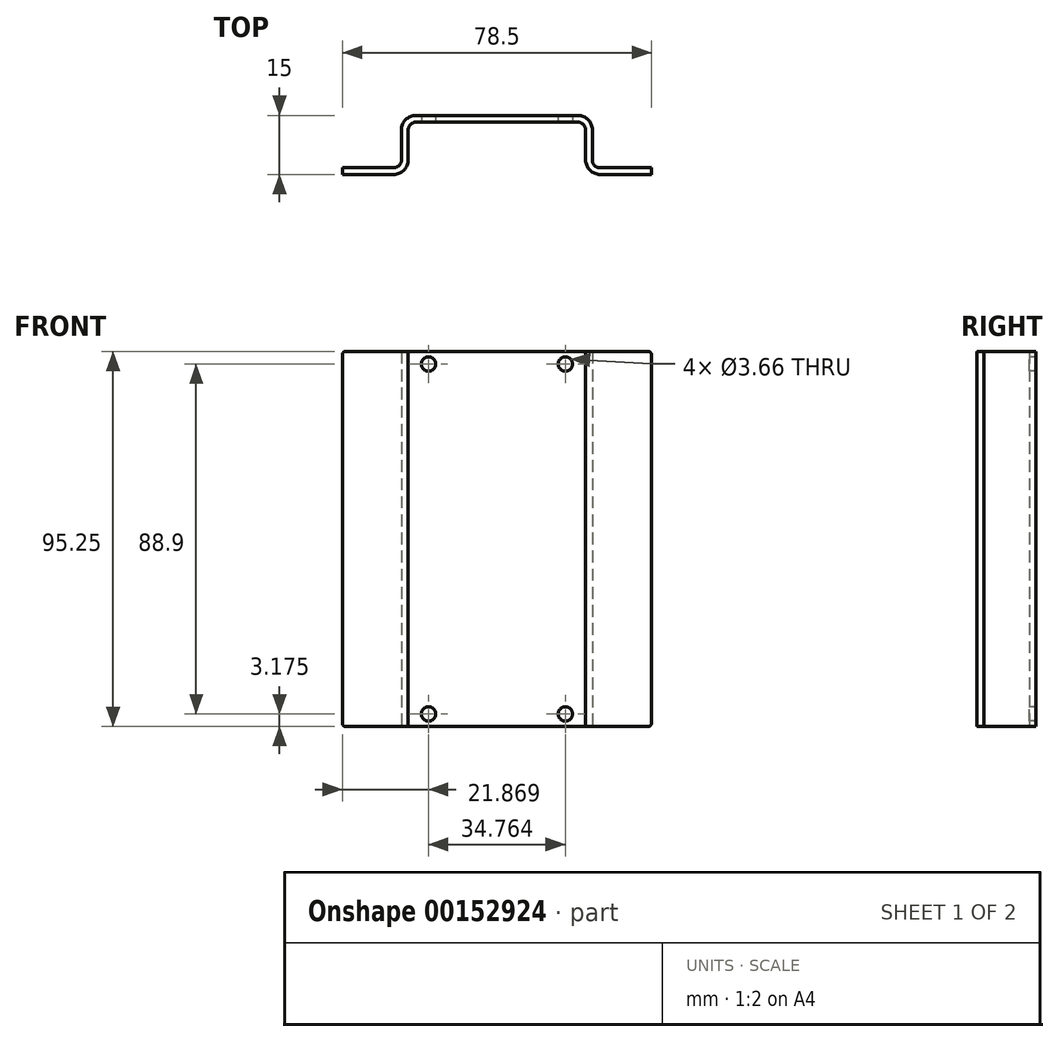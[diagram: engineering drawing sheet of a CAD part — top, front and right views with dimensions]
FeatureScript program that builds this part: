
annotation { "Feature Type Name" : "Feature", "Feature Type Description" : "" }
export const myFeature = defineFeature(function(context is Context, id is Id, definition is map)
    precondition{}
    {
        {
            var Q0;
            Q0=qCreatedBy(makeId("Top.planeOp"),FACE);
            var sketch = newSketch(context, id + "F0", { "sketchPlane" : qUnion([Q0])});
            skLineSegment(sketch, "E0.left", {"start": v(0, 0) * mm, "end": v(0, -13.3) * mm});
            skLineSegment(sketch, "E0.right", {"start": v(-1.7, 1.7) * mm, "end": v(-1.7, -11.58) * mm});
            skLineSegment(sketch, "E1.bottom", {"start": v(-1.7, -11.58) * mm, "end": v(-16.7, -11.58) * mm});
            skLineSegment(sketch, "E1.top", {"start": v(0, -13.3) * mm, "end": v(-16.7, -13.3) * mm});
            skLineSegment(sketch, "E1.right", {"start": v(-16.7, -11.58) * mm, "end": v(-16.7, -13.3) * mm});
            skLineSegment(sketch, "E2.bottom", {"start": v(0, 0) * mm, "end": v(45.08, 0) * mm});
            skLineSegment(sketch, "E2.top", {"start": v(-1.7, 1.7) * mm, "end": v(46.8, 1.7) * mm});
            skLineSegment(sketch, "E3", {"start": v(0, -6.65) * mm, "end": v(-1.7, -6.65) * mm, "construction": true});
            skLineSegment(sketch, "E4.left", {"start": v(45.08, 0) * mm, "end": v(45.08, -13.3) * mm});
            skLineSegment(sketch, "E4.right", {"start": v(46.8, 1.7) * mm, "end": v(46.8, -11.58) * mm});
            skLineSegment(sketch, "E5.bottom", {"start": v(46.8, -11.58) * mm, "end": v(61.8, -11.58) * mm});
            skLineSegment(sketch, "E5.top", {"start": v(45.08, -13.3) * mm, "end": v(61.8, -13.3) * mm});
            skLineSegment(sketch, "E5.right", {"start": v(61.8, -11.58) * mm, "end": v(61.8, -13.3) * mm});
            skLineSegment(sketch, "E6", {"start": v(45.08, -6.65) * mm, "end": v(46.8, -6.65) * mm, "construction": true});
            skLineSegment(sketch, "E7", {"start": v(22.54, 0) * mm, "end": v(22.54, 1.7) * mm, "construction": true});
            skPoint(sketch, "E8", {"position": v(-9.2, -11.58) * mm});
            skPoint(sketch, "E9", {"position": v(54.3, -11.58) * mm});
            skSolve(sketch);
        }
        {
            var Q0;
            Q0=qSketchRegion(id+"F0",true);
            extrude(context, id + "F1", {"entities" : qUnion([Q0]), "depth" : 95.25 * mm});
        }
        {
            var Q0;
            Q0=makeQuery(id+"F1.opExtrude","SWEPT_EDGE",EDGE,{"disambiguationData":[OSD([sQuery(id+"F0.wireOp",EDGE,"E0.left"),sQuery(id+"F0.wireOp",EDGE,"E2.bottom")])]});
            var Q1;
            Q1=makeQuery(id+"F1.opExtrude","SWEPT_EDGE",EDGE,{"disambiguationData":[OSD([sQuery(id+"F0.wireOp",EDGE,"E0.right"),sQuery(id+"F0.wireOp",EDGE,"E1.bottom")])]});
            var Q2;
            Q2=makeQuery(id+"F1.opExtrude","SWEPT_EDGE",EDGE,{"disambiguationData":[OSD([sQuery(id+"F0.wireOp",EDGE,"E2.bottom"),sQuery(id+"F0.wireOp",EDGE,"E4.left")])]});
            var Q3;
            Q3=makeQuery(id+"F1.opExtrude","SWEPT_EDGE",EDGE,{"disambiguationData":[OSD([sQuery(id+"F0.wireOp",EDGE,"E4.right"),sQuery(id+"F0.wireOp",EDGE,"E5.bottom")])]});
            fillet(context, id + "F2", {"entities" : qUnion([Q0, Q1, Q2, Q3]), "radius" : 1.98 * mm, "tangentPropagation" : true, "allowEdgeOverflow" : false});
        }
        {
            var Q0;
            Q0=makeQuery(id+"F1.opExtrude","SWEPT_EDGE",EDGE,{"disambiguationData":[OSD([sQuery(id+"F0.wireOp",EDGE,"E0.left"),sQuery(id+"F0.wireOp",EDGE,"E1.top")])]});
            var Q1;
            Q1=makeQuery(id+"F1.opExtrude","SWEPT_EDGE",EDGE,{"disambiguationData":[OSD([sQuery(id+"F0.wireOp",EDGE,"E0.right"),sQuery(id+"F0.wireOp",EDGE,"E2.top")])]});
            var Q2;
            Q2=makeQuery(id+"F1.opExtrude","SWEPT_EDGE",EDGE,{"disambiguationData":[OSD([sQuery(id+"F0.wireOp",EDGE,"E2.top"),sQuery(id+"F0.wireOp",EDGE,"E4.right")])]});
            var Q3;
            Q3=makeQuery(id+"F1.opExtrude","SWEPT_EDGE",EDGE,{"disambiguationData":[OSD([sQuery(id+"F0.wireOp",EDGE,"E4.left"),sQuery(id+"F0.wireOp",EDGE,"E5.top")])]});
            fillet(context, id + "F3", {"entities" : qUnion([Q0, Q1, Q2, Q3]), "radius" : 3.7 * mm, "tangentPropagation" : true, "allowEdgeOverflow" : false});
        }
        {
            var Q0;
            Q0=makeQuery(id+"F1.opExtrude","CAP_EDGE",EDGE,{"disambiguationData":[OSD([sQuery(id+"F0.wireOp",EDGE,"E1.right")])],"isStart":true});
            var Q1;
            Q1=makeQuery(id+"F1.opExtrude","CAP_EDGE",EDGE,{"disambiguationData":[OSD([sQuery(id+"F0.wireOp",EDGE,"E1.right")])],"isStart":false});
            var Q2;
            Q2=makeQuery(id+"F1.opExtrude","CAP_EDGE",EDGE,{"disambiguationData":[OSD([sQuery(id+"F0.wireOp",EDGE,"E5.right")])],"isStart":true});
            var Q3;
            Q3=makeQuery(id+"F1.opExtrude","CAP_EDGE",EDGE,{"disambiguationData":[OSD([sQuery(id+"F0.wireOp",EDGE,"E5.right")])],"isStart":false});
            fillet(context, id + "F4", {"entities" : qUnion([Q0, Q1, Q2, Q3]), "radius" : 0.76 * mm, "tangentPropagation" : true, "allowEdgeOverflow" : false});
        }
        {
            var Q0;
            Q0=makeQuery(id+"F1.opExtrude","SWEPT_FACE",FACE,{"disambiguationData":[OSD([sQuery(id+"F0.wireOp",EDGE,"E2.bottom")])]});
            var sketch = newSketch(context, id + "F5", { "sketchPlane" : qUnion([Q0])});
            skCircle(sketch, "E10", {"center": v(5.16, 92.08) * mm, "radius": 1.83 * mm});
            skCircle(sketch, "E11", {"center": v(5.16, 3.17) * mm, "radius": 1.83 * mm});
            skLineSegment(sketch, "E12", {"start": v(22.54, 0) * mm, "end": v(22.54, 95.25) * mm, "construction": true});
            skLineSegment(sketch, "E13", {"start": v(43.1, 92.08) * mm, "end": v(39.92, 92.08) * mm, "construction": true});
            skLineSegment(sketch, "E14", {"start": v(39.92, 92.08) * mm, "end": v(39.92, 95.25) * mm, "construction": true});
            skLineSegment(sketch, "E15.bottom", {"start": v(39.92, 92.08) * mm, "end": v(5.16, 92.08) * mm, "construction": true});
            skLineSegment(sketch, "E15.top", {"start": v(39.92, 3.17) * mm, "end": v(5.16, 3.17) * mm, "construction": true});
            skLineSegment(sketch, "E15.left", {"start": v(39.92, 92.08) * mm, "end": v(39.92, 3.18) * mm, "construction": true});
            skLineSegment(sketch, "E15.right", {"start": v(5.16, 92.08) * mm, "end": v(5.16, 3.17) * mm, "construction": true});
            skPoint(sketch, "E15.middle", {"position": v(22.54, 47.63) * mm});
            skCircle(sketch, "E16", {"center": v(39.92, 92.08) * mm, "radius": 1.83 * mm});
            skCircle(sketch, "E17", {"center": v(39.92, 3.18) * mm, "radius": 1.83 * mm});
            skSolve(sketch);
        }
        {
            var Q0;
            Q0=qSketchRegion(id+"F5",true);
            var Q1;
            Q1=makeQuery(id+"F1.opExtrude","SWEPT_FACE",FACE,{"disambiguationData":[OSD([sQuery(id+"F0.wireOp",EDGE,"E2.top")])]});
            extrude(context, id + "F6", {"entities" : qUnion([Q0]), "operationType" : NewBodyOperationType.REMOVE, "endBound" : BoundingType.UP_TO_SURFACE, "oppositeDirection" : true, "endBoundEntityFace" : qUnion([Q1]), "depth" : 25.4 * mm});
        }
    });
